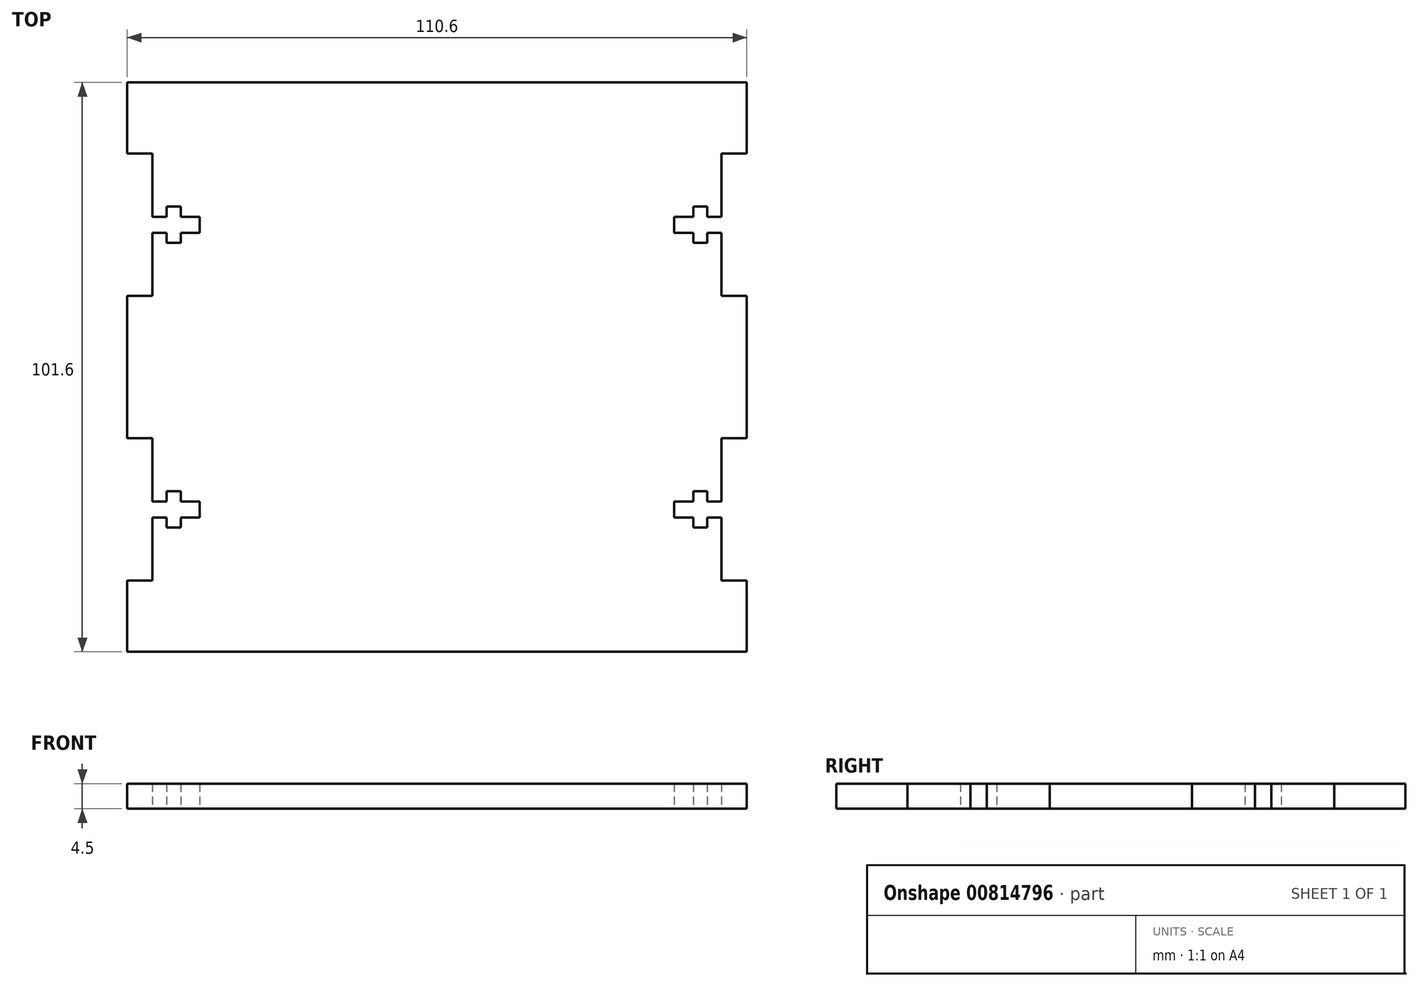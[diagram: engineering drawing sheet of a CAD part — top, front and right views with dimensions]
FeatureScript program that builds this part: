
annotation { "Feature Type Name" : "Feature", "Feature Type Description" : "" }
export const myFeature = defineFeature(function(context is Context, id is Id, definition is map)
    precondition{}
    {
        {
            var Q0;
            Q0=qCreatedBy(makeId("Top.planeOp"),FACE);
            var sketch = newSketch(context, id + "F0", { "sketchPlane" : qUnion([Q0])});
            skLineSegment(sketch, "E0.bottom", {"start": v(-50.8, 50.8) * mm, "end": v(50.8, 50.8) * mm});
            skLineSegment(sketch, "E0.top", {"start": v(-50.8, -50.8) * mm, "end": v(50.8, -50.8) * mm});
            skLineSegment(sketch, "E0.left", {"start": v(-50.8, 38.1) * mm, "end": v(-50.8, 26.85) * mm});
            skLineSegment(sketch, "E1", {"start": v(-50.8, 50.8) * mm, "end": v(50.8, -50.8) * mm, "construction": true});
            skLineSegment(sketch, "E2", {"start": v(-50.8, 50.8) * mm, "end": v(-55.3, 50.8) * mm});
            skLineSegment(sketch, "E3", {"start": v(-55.3, 50.8) * mm, "end": v(-55.3, 38.1) * mm});
            skLineSegment(sketch, "E4", {"start": v(-55.3, 38.1) * mm, "end": v(-50.8, 38.1) * mm});
            skLineSegment(sketch, "E5", {"start": v(-50.8, 12.7) * mm, "end": v(-55.3, 12.7) * mm});
            skLineSegment(sketch, "E6", {"start": v(-55.3, 12.7) * mm, "end": v(-55.3, 0) * mm});
            skLineSegment(sketch, "E7", {"start": v(-55.3, 0) * mm, "end": v(50.8, 0) * mm, "construction": true});
            skLineSegment(sketch, "E8", {"start": v(-50.8, 26.85) * mm, "end": v(-48.26, 26.85) * mm});
            skLineSegment(sketch, "E9", {"start": v(-48.26, 26.85) * mm, "end": v(-48.26, 28.64) * mm});
            skLineSegment(sketch, "E10", {"start": v(-48.26, 28.64) * mm, "end": v(-45.75, 28.64) * mm});
            skLineSegment(sketch, "E11", {"start": v(-45.75, 28.64) * mm, "end": v(-45.75, 26.85) * mm});
            skLineSegment(sketch, "E12", {"start": v(-45.75, 26.85) * mm, "end": v(-42.34, 26.85) * mm});
            skLineSegment(sketch, "E13", {"start": v(-42.34, 26.85) * mm, "end": v(-42.34, 23.95) * mm});
            skLineSegment(sketch, "E14", {"start": v(-42.34, 23.95) * mm, "end": v(-45.75, 23.95) * mm});
            skLineSegment(sketch, "E15", {"start": v(-45.75, 23.95) * mm, "end": v(-45.75, 22.16) * mm});
            skLineSegment(sketch, "E16", {"start": v(-45.75, 22.16) * mm, "end": v(-48.26, 22.16) * mm});
            skLineSegment(sketch, "E17", {"start": v(-48.26, 22.16) * mm, "end": v(-48.26, 23.95) * mm});
            skLineSegment(sketch, "E18", {"start": v(-48.26, 23.95) * mm, "end": v(-50.8, 23.95) * mm});
            skLineSegment(sketch, "E19", {"start": v(-48.26, 26.85) * mm, "end": v(-48.26, 23.95) * mm, "construction": true});
            skLineSegment(sketch, "E20", {"start": v(-45.75, 26.85) * mm, "end": v(-45.75, 23.95) * mm, "construction": true});
            skLineSegment(sketch, "E21", {"start": v(-42.34, 25.4) * mm, "end": v(-50.8, 25.4) * mm, "construction": true});
            skPoint(sketch, "E21.endSnap0", {"position": v(-45.75, 25.4) * mm});
            skLineSegment(sketch, "E22", {"start": v(-50.8, 23.95) * mm, "end": v(-50.8, 12.7) * mm});
            skPoint(sketch, "E23.MirrorCS.end.orphan", {"position": v(-55.3, 0) * mm});
            skPoint(sketch, "E24.MirrorCS.start.orphan", {"position": v(-50.8, -50.8) * mm});
            skLineSegment(sketch, "E25.MirrorCS", {"start": v(-48.26, -28.64) * mm, "end": v(-45.75, -28.64) * mm});
            skLineSegment(sketch, "E26.MirrorCS", {"start": v(-45.75, -28.64) * mm, "end": v(-45.75, -26.85) * mm});
            skLineSegment(sketch, "E27.MirrorCS", {"start": v(-48.26, -26.85) * mm, "end": v(-48.26, -28.64) * mm});
            skLineSegment(sketch, "E28.MirrorCS", {"start": v(-45.75, -26.85) * mm, "end": v(-45.75, -23.95) * mm, "construction": true});
            skLineSegment(sketch, "E29.MirrorCS", {"start": v(-45.75, -23.95) * mm, "end": v(-45.75, -22.16) * mm});
            skLineSegment(sketch, "E30.MirrorCS", {"start": v(-48.26, -23.95) * mm, "end": v(-50.8, -23.95) * mm});
            skLineSegment(sketch, "E31.MirrorCS", {"start": v(-50.8, -26.85) * mm, "end": v(-48.26, -26.85) * mm});
            skLineSegment(sketch, "E32.MirrorCS", {"start": v(-42.34, -25.4) * mm, "end": v(-50.8, -25.4) * mm, "construction": true});
            skLineSegment(sketch, "E33.MirrorCS", {"start": v(-48.26, -26.85) * mm, "end": v(-48.26, -23.95) * mm, "construction": true});
            skLineSegment(sketch, "E34.MirrorCS", {"start": v(-48.26, -22.16) * mm, "end": v(-48.26, -23.95) * mm});
            skLineSegment(sketch, "E35.MirrorCS", {"start": v(-55.3, -38.1) * mm, "end": v(-50.8, -38.1) * mm});
            skLineSegment(sketch, "E36.MirrorCS", {"start": v(-42.34, -26.85) * mm, "end": v(-42.34, -23.95) * mm});
            skLineSegment(sketch, "E37.MirrorCS", {"start": v(-45.75, -22.16) * mm, "end": v(-48.26, -22.16) * mm});
            skLineSegment(sketch, "E38.MirrorCS", {"start": v(-50.8, -50.8) * mm, "end": v(-55.3, -50.8) * mm});
            skLineSegment(sketch, "E39.MirrorCS", {"start": v(-42.34, -23.95) * mm, "end": v(-45.75, -23.95) * mm});
            skLineSegment(sketch, "E40.MirrorCS", {"start": v(-50.8, -12.7) * mm, "end": v(-55.3, -12.7) * mm});
            skLineSegment(sketch, "E41.MirrorCS", {"start": v(-45.75, -26.85) * mm, "end": v(-42.34, -26.85) * mm});
            skLineSegment(sketch, "E42.MirrorCS", {"start": v(-50.8, -23.95) * mm, "end": v(-50.8, -12.7) * mm});
            skPoint(sketch, "E43.MirrorP", {"position": v(-45.75, -25.4) * mm});
            skLineSegment(sketch, "E44.MirrorCS", {"start": v(-55.3, -50.8) * mm, "end": v(-55.3, -38.1) * mm});
            skLineSegment(sketch, "E45.MirrorCS", {"start": v(-50.8, -38.1) * mm, "end": v(-50.8, -26.85) * mm});
            skLineSegment(sketch, "E46.MirrorCS", {"start": v(-55.3, -12.7) * mm, "end": v(-55.3, 0) * mm});
            skLineSegment(sketch, "E47", {"start": v(0, 50.8) * mm, "end": v(0, -50.8) * mm, "construction": true});
            skLineSegment(sketch, "E48.MirrorCS", {"start": v(45.75, -28.64) * mm, "end": v(45.75, -26.85) * mm});
            skLineSegment(sketch, "E49.MirrorCS", {"start": v(48.26, 22.16) * mm, "end": v(48.26, 23.95) * mm});
            skLineSegment(sketch, "E50.MirrorCS", {"start": v(48.26, -26.85) * mm, "end": v(48.26, -28.64) * mm});
            skLineSegment(sketch, "E51.MirrorCS", {"start": v(45.75, 23.95) * mm, "end": v(45.75, 22.16) * mm});
            skLineSegment(sketch, "E52.MirrorCS", {"start": v(45.75, 28.64) * mm, "end": v(45.75, 26.85) * mm});
            skLineSegment(sketch, "E53.MirrorCS", {"start": v(45.75, 26.85) * mm, "end": v(42.34, 26.85) * mm});
            skLineSegment(sketch, "E54.MirrorCS", {"start": v(50.8, 26.85) * mm, "end": v(48.26, 26.85) * mm});
            skLineSegment(sketch, "E55.MirrorCS", {"start": v(45.75, -26.85) * mm, "end": v(45.75, -23.95) * mm, "construction": true});
            skLineSegment(sketch, "E56.MirrorCS", {"start": v(48.26, 26.85) * mm, "end": v(48.26, 23.95) * mm, "construction": true});
            skLineSegment(sketch, "E57.MirrorCS", {"start": v(48.26, 26.85) * mm, "end": v(48.26, 28.64) * mm});
            skLineSegment(sketch, "E58.MirrorCS", {"start": v(48.26, 28.64) * mm, "end": v(45.75, 28.64) * mm});
            skLineSegment(sketch, "E59.MirrorCS", {"start": v(42.34, 25.4) * mm, "end": v(50.8, 25.4) * mm, "construction": true});
            skLineSegment(sketch, "E60.MirrorCS", {"start": v(48.26, 23.95) * mm, "end": v(50.8, 23.95) * mm});
            skLineSegment(sketch, "E61.MirrorCS", {"start": v(42.34, 23.95) * mm, "end": v(45.75, 23.95) * mm});
            skLineSegment(sketch, "E62.MirrorCS", {"start": v(42.34, -25.4) * mm, "end": v(50.8, -25.4) * mm, "construction": true});
            skLineSegment(sketch, "E63.MirrorCS", {"start": v(45.75, 26.85) * mm, "end": v(45.75, 23.95) * mm, "construction": true});
            skLineSegment(sketch, "E64.MirrorCS", {"start": v(48.26, -26.85) * mm, "end": v(48.26, -23.95) * mm, "construction": true});
            skLineSegment(sketch, "E65.MirrorCS", {"start": v(45.75, -26.85) * mm, "end": v(42.34, -26.85) * mm});
            skLineSegment(sketch, "E66.MirrorCS", {"start": v(48.26, -28.64) * mm, "end": v(45.75, -28.64) * mm});
            skLineSegment(sketch, "E67.MirrorCS", {"start": v(50.8, -26.85) * mm, "end": v(48.26, -26.85) * mm});
            skLineSegment(sketch, "E68.MirrorCS", {"start": v(45.75, 22.16) * mm, "end": v(48.26, 22.16) * mm});
            skLineSegment(sketch, "E69.MirrorCS", {"start": v(45.75, -23.95) * mm, "end": v(45.75, -22.16) * mm});
            skLineSegment(sketch, "E70.MirrorCS", {"start": v(45.75, -22.16) * mm, "end": v(48.26, -22.16) * mm});
            skLineSegment(sketch, "E71.MirrorCS", {"start": v(48.26, -23.95) * mm, "end": v(50.8, -23.95) * mm});
            skLineSegment(sketch, "E72.MirrorCS", {"start": v(42.34, -23.95) * mm, "end": v(45.75, -23.95) * mm});
            skLineSegment(sketch, "E73.MirrorCS", {"start": v(48.26, -22.16) * mm, "end": v(48.26, -23.95) * mm});
            skLineSegment(sketch, "E74.MirrorCS", {"start": v(55.3, -38.1) * mm, "end": v(50.8, -38.1) * mm});
            skLineSegment(sketch, "E75.MirrorCS", {"start": v(55.3, 38.1) * mm, "end": v(50.8, 38.1) * mm});
            skLineSegment(sketch, "E76.MirrorCS", {"start": v(50.8, -12.7) * mm, "end": v(55.3, -12.7) * mm});
            skLineSegment(sketch, "E77.MirrorCS", {"start": v(50.8, 50.8) * mm, "end": v(55.3, 50.8) * mm});
            skLineSegment(sketch, "E78.MirrorCS", {"start": v(50.8, 12.7) * mm, "end": v(55.3, 12.7) * mm});
            skLineSegment(sketch, "E79.MirrorCS", {"start": v(50.8, -50.8) * mm, "end": v(55.3, -50.8) * mm});
            skLineSegment(sketch, "E80.MirrorCS", {"start": v(50.8, 23.95) * mm, "end": v(50.8, 12.7) * mm});
            skPoint(sketch, "E81.MirrorP", {"position": v(55.3, 0) * mm});
            skLineSegment(sketch, "E82.MirrorCS", {"start": v(50.8, -23.95) * mm, "end": v(50.8, -12.7) * mm});
            skLineSegment(sketch, "E83.MirrorCS", {"start": v(50.8, 38.1) * mm, "end": v(50.8, 26.85) * mm});
            skLineSegment(sketch, "E84.MirrorCS", {"start": v(55.3, 12.7) * mm, "end": v(55.3, 0) * mm});
            skLineSegment(sketch, "E85.MirrorCS", {"start": v(55.3, -12.7) * mm, "end": v(55.3, 0) * mm});
            skPoint(sketch, "E86.MirrorP", {"position": v(45.75, 25.4) * mm});
            skPoint(sketch, "E87.MirrorP", {"position": v(45.75, -25.4) * mm});
            skLineSegment(sketch, "E88.MirrorCS", {"start": v(50.8, -38.1) * mm, "end": v(50.8, -26.85) * mm});
            skLineSegment(sketch, "E89.MirrorCS", {"start": v(55.3, 50.8) * mm, "end": v(55.3, 38.1) * mm});
            skLineSegment(sketch, "E90.MirrorCS", {"start": v(55.3, -50.8) * mm, "end": v(55.3, -38.1) * mm});
            skPoint(sketch, "E91.MirrorP", {"position": v(50.8, -50.8) * mm});
            skLineSegment(sketch, "E92.MirrorCS", {"start": v(42.34, 26.85) * mm, "end": v(42.34, 23.95) * mm});
            skLineSegment(sketch, "E93.MirrorCS", {"start": v(42.34, -26.85) * mm, "end": v(42.34, -23.95) * mm});
            skSolve(sketch);
        }
        {
            var Q0;
            Q0 = qSketchRegion(id + "F0", true);
            extrude(context, id + "F1", {"entities" : qUnion([Q0]), "depth" : 4.5 * mm, "offsetDistance" : 25.4 * mm});
        }
    });
